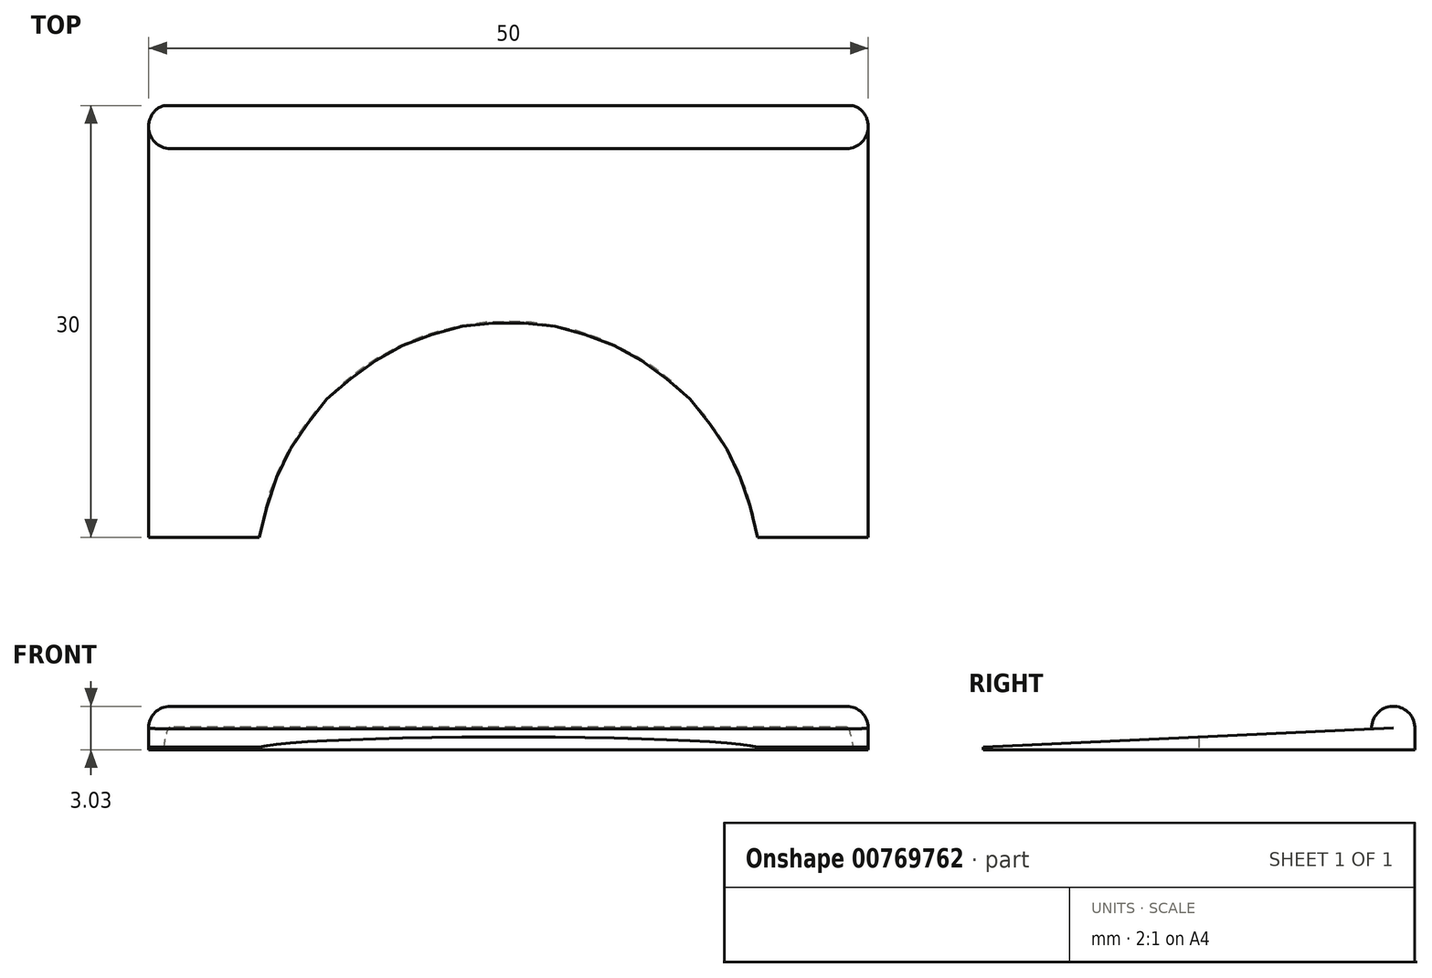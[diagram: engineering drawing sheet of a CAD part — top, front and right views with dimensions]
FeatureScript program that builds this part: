
annotation { "Feature Type Name" : "Feature", "Feature Type Description" : "" }
export const myFeature = defineFeature(function(context is Context, id is Id, definition is map)
    precondition{}
    {
        {
            var Q0;
            Q0=qCreatedBy(makeId("Right.planeOp"),FACE);
            var sketch = newSketch(context, id + "F0", { "sketchPlane" : qUnion([Q0])});
            skLineSegment(sketch, "E0", {"start": v(-15, 0) * mm, "end": v(-15, 0.2) * mm});
            skLineSegment(sketch, "E1", {"start": v(-15, 0.2) * mm, "end": v(15, 1.6) * mm});
            skLineSegment(sketch, "E2", {"start": v(15, 1.6) * mm, "end": v(15, 0) * mm});
            skLineSegment(sketch, "E3", {"start": v(15, 0) * mm, "end": v(-15, 0) * mm});
            skSolve(sketch);
        }
        {
            var Q0;
            Q0=makeQuery(id+"F0.imprint","IMPRINT",FACE,{"disambiguationData":[TD([[makeQuery(id+"F0.imprint","IMPRINT",EDGE,{"derivedFrom":sQuery(id+"F0.wireOp",EDGE,"E0")}),-1.0]])]});
            extrude(context, id + "F1", {"entities" : qUnion([Q0]), "endBound" : BoundingType.SYMMETRIC, "depth" : 50 * mm, "offsetDistance" : 25 * mm});
        }
        {
            var Q0;
            Q0=makeQuery(id+"F1.opExtrude","SWEPT_FACE",FACE,{"disambiguationData":[OSD([sQuery(id+"F0.wireOp",EDGE,"E3")])]});
            var sketch = newSketch(context, id + "F2", { "sketchPlane" : qUnion([Q0])});
            skCircle(sketch, "E4", {"center": v(0, 17.5) * mm, "radius": 17.5 * mm});
            skLineSegment(sketch, "E5", {"start": v(17.32, 15) * mm, "end": v(25, 15) * mm, "construction": true});
            skPoint(sketch, "E6", {"position": v(0, 15) * mm});
            skSolve(sketch);
        }
        {
            var Q0;
            Q0 = qSketchRegion(id + "F2", true);
            extrude(context, id + "F3", {"entities" : qUnion([Q0]), "operationType" : NewBodyOperationType.REMOVE, "oppositeDirection" : true, "depth" : 25 * mm, "offsetDistance" : 25 * mm});
        }
        {
            var Q0;
            Q0=makeQuery(id+"F1.opExtrude","SWEPT_FACE",FACE,{"disambiguationData":[OSD([sQuery(id+"F0.wireOp",EDGE,"E1")])]});
            var sketch = newSketch(context, id + "F4", { "sketchPlane" : qUnion([Q0])});
            skLineSegment(sketch, "E7", {"start": v(-25, 15.06) * mm, "end": v(-25, 12.06) * mm});
            skLineSegment(sketch, "E8", {"start": v(-25, 12.06) * mm, "end": v(25, 12.06) * mm});
            skLineSegment(sketch, "E9", {"start": v(25, 12.06) * mm, "end": v(25, 15.06) * mm});
            skSolve(sketch);
        }
        {
            var Q0;
            Q0=makeQuery(id+"F4.imprint","IMPRINT",FACE,{"disambiguationData":[TD([[makeQuery(id+"F4.imprint","IMPRINT",EDGE,{"derivedFrom":sQuery(id+"F4.wireOp",EDGE,"E7")}),-1.0]])]});
            extrude(context, id + "F5", {"entities" : qUnion([Q0]), "operationType" : NewBodyOperationType.ADD, "depth" : 1.5 * mm, "offsetDistance" : 25 * mm});
        }
        {
            var Q0;
            Q0=makeQuery(id+"F5.opExtrude","SWEPT_EDGE",EDGE,{"disambiguationData":[OSD([sQuery(id+"F0.wireOp",EDGE,"E1"),sQuery(id+"F4.wireOp",EDGE,"E7"),sQuery(id+"F4.wireOp",EDGE,"E8")])]});
            var Q1;
            Q1=makeQuery(id+"F5.opExtrude","SWEPT_EDGE",EDGE,{"disambiguationData":[OSD([sQuery(id+"F0.wireOp",EDGE,"E1"),sQuery(id+"F0.wireOp",EDGE,"E2"),sQuery(id+"F4.wireOp",EDGE,"E7")])]});
            var Q2;
            Q2=makeQuery(id+"F5.opExtrude","SWEPT_EDGE",EDGE,{"disambiguationData":[OSD([sQuery(id+"F0.wireOp",EDGE,"E1"),sQuery(id+"F0.wireOp",EDGE,"E2"),sQuery(id+"F4.wireOp",EDGE,"E9")])]});
            var Q3;
            Q3=makeQuery(id+"F5.opExtrude","SWEPT_EDGE",EDGE,{"disambiguationData":[OSD([sQuery(id+"F0.wireOp",EDGE,"E1"),sQuery(id+"F4.wireOp",EDGE,"E8"),sQuery(id+"F4.wireOp",EDGE,"E9")])]});
            var Q4;
            Q4=makeQuery(id+"F5.opExtrude","CAP_FACE",FACE,{"disambiguationData":[OSD([sQuery(id+"F0.wireOp",EDGE,"E1"),sQuery(id+"F0.wireOp",EDGE,"E2"),sQuery(id+"F4.wireOp",EDGE,"E7"),sQuery(id+"F4.wireOp",EDGE,"E8"),sQuery(id+"F4.wireOp",EDGE,"E9")])],"isStart":false});
            fillet(context, id + "F6", {"entities" : qUnion([Q0, Q1, Q2, Q3, Q4]), "tangentPropagation" : true, "radius" : 1.5 * mm, "defaultsChanged" : false, "vertexSettings" : [], "allowEdgeOverflow" : false});
        }
    });
